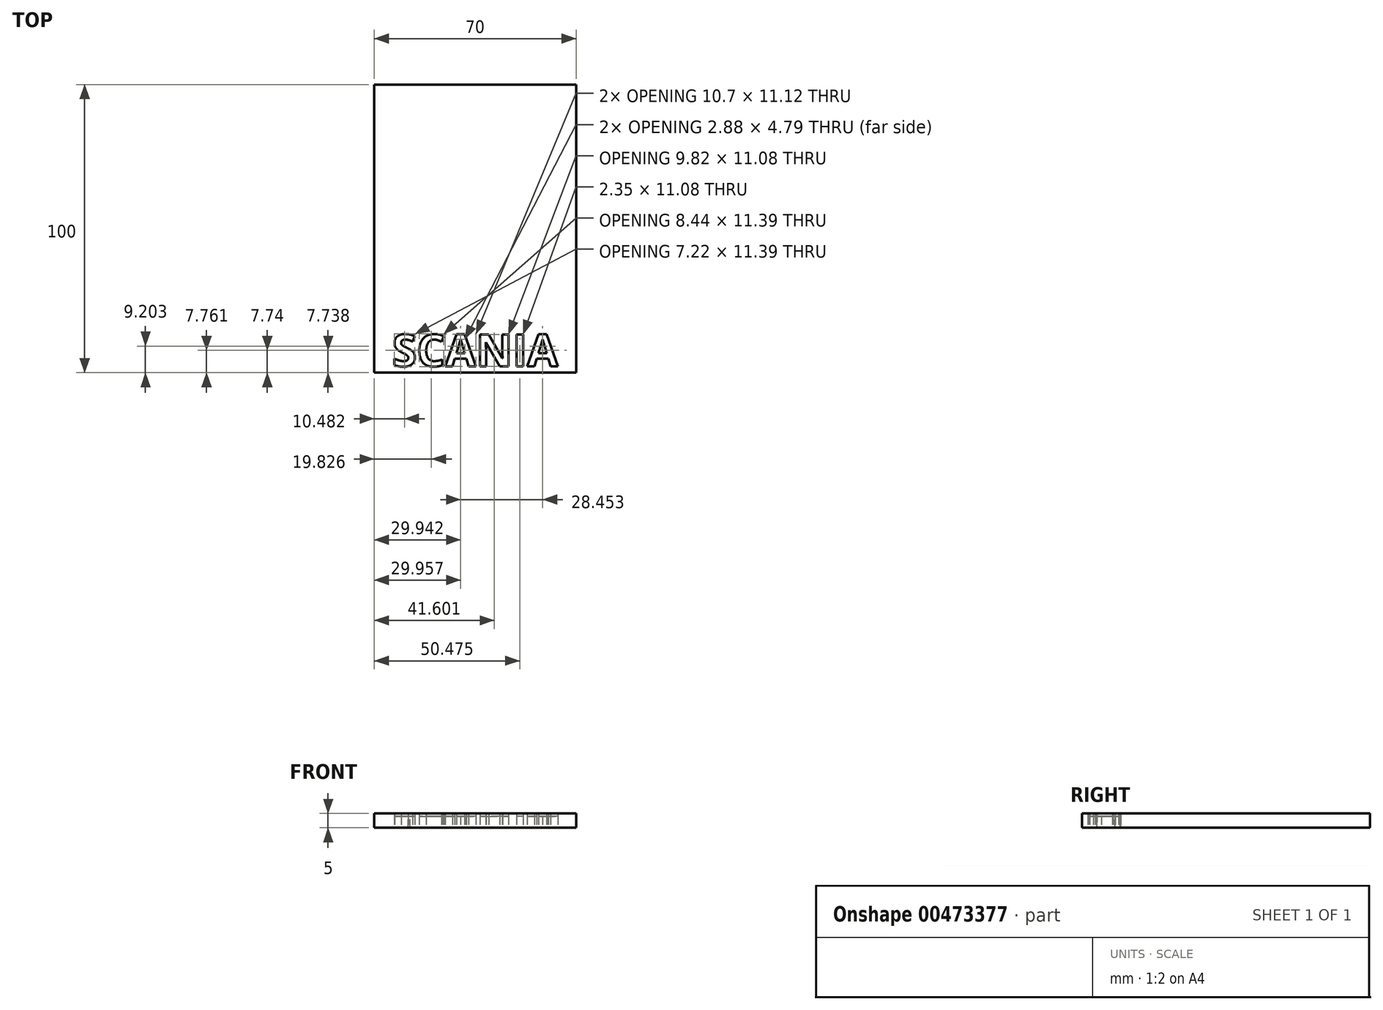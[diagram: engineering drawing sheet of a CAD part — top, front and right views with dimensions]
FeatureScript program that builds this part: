
annotation { "Feature Type Name" : "Feature", "Feature Type Description" : "" }
export const myFeature = defineFeature(function(context is Context, id is Id, definition is map)
    precondition{}
    {
        {
            var Q0;
            Q0=qCreatedBy(makeId("Top.planeOp"),FACE);
            var sketch = newSketch(context, id + "F0", { "sketchPlane" : qUnion([Q0])});
            skLineSegment(sketch, "E0.bottom", {"start": v(0, 0) * mm, "end": v(70, 0) * mm});
            skLineSegment(sketch, "E0.top", {"start": v(0, 100) * mm, "end": v(70, 100) * mm});
            skLineSegment(sketch, "E0.left", {"start": v(0, 0) * mm, "end": v(0, 100) * mm});
            skLineSegment(sketch, "E0.right", {"start": v(70, 0) * mm, "end": v(70, 100) * mm});
            skText(sketch, "E1", { "text": "SCANIA", "fontName": "OpenSans-Bold.ttf"});
            const initialGuessF0  = {"E1": [0.00616, 0.0022, 1, 0, 0.01117]};
            skSetInitialGuess(sketch, initialGuessF0);
            skSolve(sketch);
        }
        {
            var Q0;
            Q0=makeQuery(id+"F0.imprint","IMPRINT",FACE,{"disambiguationData":[TD([[makeQuery(id+"F0.imprint","IMPRINT",EDGE,{"derivedFrom":sQuery(id+"F0.wireOp",EDGE,"E1.sketch_text.stroke-55")}),-1.0]])]});
            var Q1;
            Q1=makeQuery(id+"F0.imprint","IMPRINT",FACE,{"disambiguationData":[TD([[makeQuery(id+"F0.imprint","IMPRINT",EDGE,{"derivedFrom":sQuery(id+"F0.wireOp",EDGE,"E1.sketch_text.stroke-69")}),-1.0]])]});
            var Q2;
            Q2=makeQuery(id+"F0.imprint","IMPRINT",FACE,{"disambiguationData":[TD([[makeQuery(id+"F0.imprint","IMPRINT",EDGE,{"derivedFrom":sQuery(id+"F0.wireOp",EDGE,"E1.sketch_text.stroke-43")}),-1.0]])]});
            var Q3;
            Q3=makeQuery(id+"F0.imprint","IMPRINT",FACE,{"disambiguationData":[TD([[makeQuery(id+"F0.imprint","IMPRINT",EDGE,{"derivedFrom":sQuery(id+"F0.wireOp",EDGE,"E1.sketch_text.stroke-28")}),-1.0]])]});
            var Q4;
            Q4=makeQuery(id+"F0.imprint","IMPRINT",FACE,{"disambiguationData":[TD([[makeQuery(id+"F0.imprint","IMPRINT",EDGE,{"derivedFrom":sQuery(id+"F0.wireOp",EDGE,"E1.sketch_text.stroke-0")}),-1.0]])]});
            var Q5;
            Q5=makeQuery(id+"F0.imprint","IMPRINT",FACE,{"disambiguationData":[TD([[makeQuery(id+"F0.imprint","IMPRINT",EDGE,{"derivedFrom":sQuery(id+"F0.wireOp",EDGE,"E1.sketch_text.stroke-73")}),-1.0]])]});
            extrude(context, id + "F1", {"entities" : qUnion([Q0, Q1, Q2, Q3, Q4, Q5]), "depth" : 4 * mm});
        }
        {
            var Q0;
            Q0=makeQuery(id+"F0.imprint","IMPRINT",FACE,{"disambiguationData":[TD([[makeQuery(id+"F0.imprint","IMPRINT",EDGE,{"derivedFrom":sQuery(id+"F0.wireOp",EDGE,"E0.bottom")}),1.0]])]});
            extrude(context, id + "F2", {"entities" : qUnion([Q0]), "depth" : 5 * mm});
        }
    });
